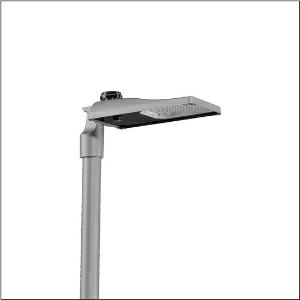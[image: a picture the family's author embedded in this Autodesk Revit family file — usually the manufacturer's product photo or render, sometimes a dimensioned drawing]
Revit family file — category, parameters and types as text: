
# Revit family: streetlight_sl_31_mini___st1_0a_5xh6d3bm08ga_d2dc
name_source: partatom
category: Lighting Fixtures
units: mm (PartAtom-declared; Revit-internal decimal feet)

## family parameters
Cut with Voids When Loaded = No
Host = Face
Light Source = No
Part Type = Normal
Room Calculation Point = No
Round Connector Dimension = Use Diameter
Shared = No

## types (1)
- --- (1 x LED, 5880 lm, 39.3 W, 3000K)
    Apparent Load = 39 VA
    CIE Flux Codes = 37 72 97 100 100
    Color Rendering = 70
    Color Temperature = 3000K
    Default Elevation = 1800 mm
    Description = Streetlight SL 31 mini NEMA (7pin) mast luminaire for post-top, side-entry; light control with lens of PMMA; light distribution: ST1.0a, direct asymmetric distribution, for standard-compliant lighting for roads and squares; LED: luminous flux: 5.880lm, light colour: 730, colour temperature: 3000K; luminous efficacy: 149,6lm/W; control: pre-setting: linear dimming characteristic, flexible luminous flux parameterisation, time-dependent luminous flux control, constant luminous flux control, intelligent temperature release in ECG and LED module, overheat protection; luminaire housing, of diecast aluminium, SITECO metallic grey (DB 702S), corrosivity category C5 high according to DIN EN ISO 12944; cover of toughened safety glass, transparent, opened without tools; mast flange of diecast aluminium, SITECO metallic grey (DB 702S), spigot size: 76/60mm, mast flange included unmounted; cable length: 6,5m, connection cable pre-assembled; mains connection: 220..240V, AC, 50/60Hz; power consumption (at start of service life): 39,3W / (at end of service life): 40,7W / (with reduced operation 50%): 18,1W; protection rating (complete): IP66; insulation class (complete): insulation class I (protective earthing); impact resistance: IK09; certification: CE, ENEC, ENEC+, VDE, UKCA; permissible operating ambient temperature for outdoor applications: -40..+50°C; packaging unit: 1 piece

Light Distribution: ST1.0a
    Height = 76 mm
    Lamp = 1 x LED
    Lamp Light Flux = 5880 lm
    Lamp Power = 39.3 W
    Lamp count = 1
    Length = 547 mm
    Luminous efficacy = 150 lm/W
    Manufacturer = Siteco
    ModVariant = No
    Model = 5XH6D3BM08GA
    Mounting Place = Pole
    Mounting Type = Pole top
    Number of Poles = 1
    OnlyDefault = Yes
    Power Factor = 1
    Product Name = Streetlight SL 31 mini | ST1.0a
    Product group = mast luminaire | pylon top
    ProductGroupID = 6100
    Protection Class = Protection class I
    Protection Degree = IP 66
    RLX_Detail_Level = 1
    RLX_Emergency_Light_Flux = 0 lm
    RLX_Emergency_Type = 0
    RLX_Emergency_Type_DB = No
    RlxData = <blob elided: 40289 chars, md5=cb889026>
    Socket = socket
    Standby Power = 0 W
    System Light Flux = 5880 lm
    System Power = 39 W
    Type Comments = factory setting: luminous flux: 100 % | dim-lin: 254 | 798 mA
    Type Image = l_1300324.jpg
    URL = http://relux.com
    VarID = @adj_061911
    Voltage = 0 V
    Weight = 0.00 kg
    Width = 265 mm

## geometry (parser evidence)
native form markers: Blend x4, Sweep x10
no freeform markers — native parametric forms only
